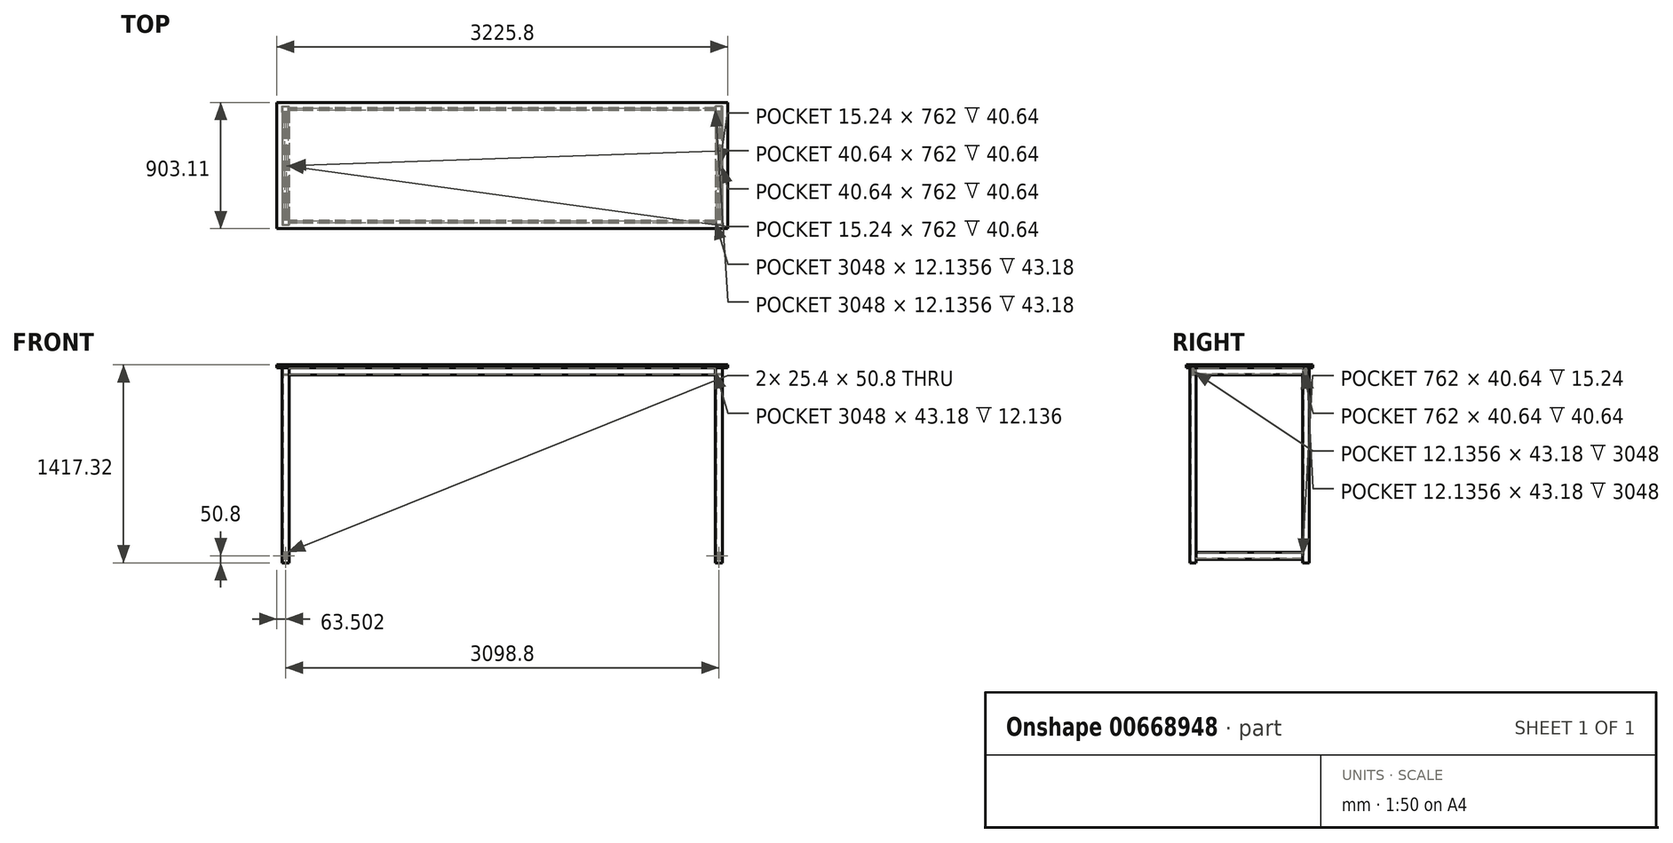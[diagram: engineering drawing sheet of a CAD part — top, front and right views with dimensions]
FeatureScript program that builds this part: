
annotation { "Feature Type Name" : "Feature", "Feature Type Description" : "" }
export const myFeature = defineFeature(function(context is Context, id is Id, definition is map)
    precondition{}
    {
        {
            var Q0;
            Q0=qCreatedBy(makeId("Top.planeOp"),FACE);
            var sketch = newSketch(context, id + "F0", { "sketchPlane" : qUnion([Q0])});
            skLineSegment(sketch, "E0.bottom", {"start": v(-52.67, 8.27) * mm, "end": v(-1.87, 8.27) * mm});
            skLineSegment(sketch, "E0.top", {"start": v(-52.67, -36.88) * mm, "end": v(-1.87, -36.88) * mm});
            skLineSegment(sketch, "E0.left", {"start": v(-52.67, 8.27) * mm, "end": v(-52.67, -36.88) * mm});
            skLineSegment(sketch, "E0.right", {"start": v(-1.87, 8.27) * mm, "end": v(-1.87, -36.88) * mm});
            skLineSegment(sketch, "E1.bottom", {"start": v(-47.59, 3.2) * mm, "end": v(-6.95, 3.2) * mm});
            skLineSegment(sketch, "E1.top", {"start": v(-47.59, -31.8) * mm, "end": v(-6.95, -31.8) * mm});
            skLineSegment(sketch, "E1.left", {"start": v(-47.59, 3.2) * mm, "end": v(-47.59, -31.8) * mm});
            skLineSegment(sketch, "E1.right", {"start": v(-6.95, 3.2) * mm, "end": v(-6.95, -31.8) * mm});
            skSolve(sketch);
        }
        {
            var Q0;
            Q0=makeQuery(id+"F0.imprint","IMPRINT",FACE,{"disambiguationData":[TD([[makeQuery(id+"F0.imprint","IMPRINT",EDGE,{"derivedFrom":sQuery(id+"F0.wireOp",EDGE,"E0.bottom")}),-1.0]])]});
            extrude(context, id + "F1", {"entities" : qUnion([Q0]), "depth" : 1397 * mm, "offsetDistance" : 25.4 * mm});
        }
        {
            var Q0;
            Q0=makeQuery(id+"F1.opExtrude","SWEPT_FACE",FACE,{"disambiguationData":[OSD([sQuery(id+"F0.wireOp",EDGE,"E0.bottom")])]});
            var sketch = newSketch(context, id + "F2", { "sketchPlane" : qUnion([Q0])});
            skLineSegment(sketch, "E2.bottom", {"start": v(14.57, 76.2) * mm, "end": v(39.97, 76.2) * mm});
            skLineSegment(sketch, "E2.top", {"start": v(14.57, 25.4) * mm, "end": v(39.97, 25.4) * mm});
            skLineSegment(sketch, "E2.left", {"start": v(14.57, 76.2) * mm, "end": v(14.57, 25.4) * mm});
            skLineSegment(sketch, "E2.right", {"start": v(39.97, 76.2) * mm, "end": v(39.97, 25.4) * mm});
            skLineSegment(sketch, "E3.bottom", {"start": v(19.65, 71.12) * mm, "end": v(34.89, 71.12) * mm});
            skLineSegment(sketch, "E3.top", {"start": v(19.65, 30.48) * mm, "end": v(34.89, 30.48) * mm});
            skLineSegment(sketch, "E3.left", {"start": v(19.65, 71.12) * mm, "end": v(19.65, 30.48) * mm});
            skLineSegment(sketch, "E3.right", {"start": v(34.89, 71.12) * mm, "end": v(34.89, 30.48) * mm});
            skLineSegment(sketch, "E4.bottom", {"start": v(52.67, 1397) * mm, "end": v(1.87, 1397) * mm});
            skLineSegment(sketch, "E4.top", {"start": v(52.67, 1346.2) * mm, "end": v(1.87, 1346.2) * mm});
            skLineSegment(sketch, "E4.left", {"start": v(52.67, 1397) * mm, "end": v(52.67, 1346.2) * mm});
            skLineSegment(sketch, "E4.right", {"start": v(1.87, 1397) * mm, "end": v(1.87, 1346.2) * mm});
            skLineSegment(sketch, "E5.bottom", {"start": v(47.59, 1391.92) * mm, "end": v(6.95, 1391.92) * mm});
            skLineSegment(sketch, "E5.top", {"start": v(47.59, 1351.28) * mm, "end": v(6.95, 1351.28) * mm});
            skLineSegment(sketch, "E5.left", {"start": v(47.59, 1391.92) * mm, "end": v(47.59, 1351.28) * mm});
            skLineSegment(sketch, "E5.right", {"start": v(6.95, 1391.92) * mm, "end": v(6.95, 1351.28) * mm});
            skSolve(sketch);
        }
        {
            var Q0;
            Q0=makeQuery(id+"F2.imprint","IMPRINT",FACE,{"disambiguationData":[TD([[makeQuery(id+"F2.imprint","IMPRINT",EDGE,{"derivedFrom":sQuery(id+"F2.wireOp",EDGE,"E2.bottom")}),-1.0]])]});
            var Q1;
            Q1=makeQuery(id+"F2.imprint","IMPRINT",FACE,{"disambiguationData":[TD([[makeQuery(id+"F2.imprint","IMPRINT",EDGE,{"derivedFrom":sQuery(id+"F2.wireOp",EDGE,"E4.bottom")}),1.0]])]});
            extrude(context, id + "F3", {"entities" : qUnion([Q0, Q1]), "operationType" : NewBodyOperationType.ADD, "depth" : 381 * mm, "offsetDistance" : 25.4 * mm});
        }
        {
            var Q0;
            Q0=makeQuery(id+"F3.boolean.opBoolean","MERGE",FACE,{"derivedFrom":[makeQuery(id+"F1.opExtrude","SWEPT_FACE",FACE,{"disambiguationData":[OSD([sQuery(id+"F0.wireOp",EDGE,"E0.right")])]}),makeQuery(id+"F3.opExtrude","SWEPT_FACE",FACE,{"disambiguationData":[OSD([sQuery(id+"F2.wireOp",EDGE,"E4.right")])]})]});
            var sketch = newSketch(context, id + "F4", { "sketchPlane" : qUnion([Q0])});
            skLineSegment(sketch, "E6.bottom", {"start": v(-24.18, 1397) * mm, "end": v(-4.43, 1397) * mm});
            skLineSegment(sketch, "E6.top", {"start": v(-24.18, 1346.2) * mm, "end": v(-4.43, 1346.2) * mm});
            skLineSegment(sketch, "E6.left", {"start": v(-24.18, 1397) * mm, "end": v(-24.18, 1346.2) * mm});
            skLineSegment(sketch, "E6.right", {"start": v(-4.43, 1397) * mm, "end": v(-4.43, 1346.2) * mm});
            skLineSegment(sketch, "E7.bottom", {"start": v(-20.37, 1393.2) * mm, "end": v(-8.24, 1393.2) * mm});
            skLineSegment(sketch, "E7.top", {"start": v(-20.37, 1350.01) * mm, "end": v(-8.24, 1350.01) * mm});
            skLineSegment(sketch, "E7.left", {"start": v(-20.37, 1393.2) * mm, "end": v(-20.37, 1350.01) * mm});
            skLineSegment(sketch, "E7.right", {"start": v(-8.24, 1393.2) * mm, "end": v(-8.24, 1350.01) * mm});
            skSolve(sketch);
        }
        {
            var Q0;
            Q0=makeQuery(id+"F4.imprint","IMPRINT",FACE,{"disambiguationData":[TD([[makeQuery(id+"F4.imprint","IMPRINT",EDGE,{"derivedFrom":sQuery(id+"F4.wireOp",EDGE,"E6.bottom")}),1.0]])]});
            extrude(context, id + "F5", {"entities" : qUnion([Q0]), "operationType" : NewBodyOperationType.ADD, "depth" : 1524 * mm, "offsetDistance" : 25.4 * mm});
        }
        {
            var Q0;
            Q0=makeQuery(id+"F1.opExtrude","SWEPT_BODY",BODY,{"disambiguationData":[OSD([sQuery(id+"F0.wireOp",EDGE,"E0.bottom"),sQuery(id+"F0.wireOp",EDGE,"E0.top"),sQuery(id+"F0.wireOp",EDGE,"E0.left"),sQuery(id+"F0.wireOp",EDGE,"E0.right"),sQuery(id+"F0.wireOp",EDGE,"E1.bottom"),sQuery(id+"F0.wireOp",EDGE,"E1.top"),sQuery(id+"F0.wireOp",EDGE,"E1.left"),sQuery(id+"F0.wireOp",EDGE,"E1.right")])]});
            var Q1;
            Q1=makeQuery(id+"F5.opExtrude","CAP_FACE",FACE,{"disambiguationData":[OSD([sQuery(id+"F4.wireOp",EDGE,"E6.bottom"),sQuery(id+"F4.wireOp",EDGE,"E6.top"),sQuery(id+"F4.wireOp",EDGE,"E6.left"),sQuery(id+"F4.wireOp",EDGE,"E6.right"),sQuery(id+"F4.wireOp",EDGE,"E7.bottom"),sQuery(id+"F4.wireOp",EDGE,"E7.top"),sQuery(id+"F4.wireOp",EDGE,"E7.left"),sQuery(id+"F4.wireOp",EDGE,"E7.right")])],"isStart":false});
            mirror(context, id + "F6", {"operationType" : NewBodyOperationType.ADD, "entities" : qUnion([Q0]), "mirrorPlane" : qUnion([Q1])});
        }
        {
            var Q0;
            Q0=makeQuery(id+"F1.opExtrude","SWEPT_BODY",BODY,{"disambiguationData":[OSD([sQuery(id+"F0.wireOp",EDGE,"E0.bottom"),sQuery(id+"F0.wireOp",EDGE,"E0.top"),sQuery(id+"F0.wireOp",EDGE,"E0.left"),sQuery(id+"F0.wireOp",EDGE,"E0.right"),sQuery(id+"F0.wireOp",EDGE,"E1.bottom"),sQuery(id+"F0.wireOp",EDGE,"E1.top"),sQuery(id+"F0.wireOp",EDGE,"E1.left"),sQuery(id+"F0.wireOp",EDGE,"E1.right")])]});
            var Q1;
            Q1=makeQuery(id+"F3.opExtrude","CAP_FACE",FACE,{"disambiguationData":[OSD([sQuery(id+"F2.wireOp",EDGE,"E4.bottom"),sQuery(id+"F2.wireOp",EDGE,"E4.top"),sQuery(id+"F2.wireOp",EDGE,"E4.left"),sQuery(id+"F2.wireOp",EDGE,"E4.right"),sQuery(id+"F2.wireOp",EDGE,"E5.bottom"),sQuery(id+"F2.wireOp",EDGE,"E5.top"),sQuery(id+"F2.wireOp",EDGE,"E5.left"),sQuery(id+"F2.wireOp",EDGE,"E5.right")])],"isStart":false});
            mirror(context, id + "F7", {"operationType" : NewBodyOperationType.ADD, "entities" : qUnion([Q0]), "mirrorPlane" : qUnion([Q1])});
        }
        {
            var Q0;
            {var subQ0=makeQuery(id+"F5.boolean.opBoolean","MERGE",FACE,{"derivedFrom":[makeQuery(id+"F3.boolean.opBoolean","MERGE",FACE,{"derivedFrom":[makeQuery(id+"F1.opExtrude","CAP_FACE",FACE,{"disambiguationData":[OSD([sQuery(id+"F0.wireOp",EDGE,"E0.bottom"),sQuery(id+"F0.wireOp",EDGE,"E0.top"),sQuery(id+"F0.wireOp",EDGE,"E0.left"),sQuery(id+"F0.wireOp",EDGE,"E0.right"),sQuery(id+"F0.wireOp",EDGE,"E1.bottom"),sQuery(id+"F0.wireOp",EDGE,"E1.top"),sQuery(id+"F0.wireOp",EDGE,"E1.left"),sQuery(id+"F0.wireOp",EDGE,"E1.right")])],"isStart":false}),makeQuery(id+"F3.opExtrude","SWEPT_FACE",FACE,{"disambiguationData":[OSD([sQuery(id+"F2.wireOp",EDGE,"E4.bottom")])]})]}),makeQuery(id+"F5.opExtrude","SWEPT_FACE",FACE,{"disambiguationData":[OSD([sQuery(id+"F4.wireOp",EDGE,"E6.bottom")])]})]});var subQ1=makeQuery(id+"F6.boolean.opBoolean","MERGE",FACE,{"derivedFrom":[subQ0,makeQuery(id+"F6.opPattern","COPY",FACE,{"derivedFrom":subQ0,"instanceName":"1"})]});Q0=makeQuery(id+"F7.boolean.opBoolean","MERGE",FACE,{"derivedFrom":[subQ1,makeQuery(id+"F7.opPattern","COPY",FACE,{"derivedFrom":subQ1,"instanceName":"1"})]});}
            var sketch = newSketch(context, id + "F8", { "sketchPlane" : qUnion([Q0])});
            skLineSegment(sketch, "E8.bottom", {"start": v(3135.03, -62.28) * mm, "end": v(-90.77, -62.28) * mm});
            skLineSegment(sketch, "E8.top", {"start": v(3135.03, 840.83) * mm, "end": v(-90.77, 840.83) * mm});
            skLineSegment(sketch, "E8.left", {"start": v(3135.03, -62.28) * mm, "end": v(3135.03, 840.83) * mm});
            skLineSegment(sketch, "E8.right", {"start": v(-90.77, -62.28) * mm, "end": v(-90.77, 840.83) * mm});
            skSolve(sketch);
        }
        {
            var Q0;
            Q0=makeQuery(id+"F8.imprint","IMPRINT",FACE,{"disambiguationData":[TD([[makeQuery(id+"F8.imprint","IMPRINT",EDGE,{"derivedFrom":sQuery(id+"F8.wireOp",EDGE,"E8.bottom")}),-1.0]])]});
            var Q1;
            {var subQ3=sQuery(id+"F0.wireOp",EDGE,"E0.top");var subQ4=makeQuery(id+"F1.opExtrude","CAP_EDGE",EDGE,{"disambiguationData":[OSD([subQ3])],"isStart":false});Q1=makeQuery(id+"F8.imprint","IMPRINT",FACE,{"disambiguationData":[TD([[makeQuery(id+"F8.imprint","IMPRINT",EDGE,{"derivedFrom":subQ4}),1.0]])]});}
            var Q2;
            {var subQ0=sQuery(id+"F4.wireOp",EDGE,"E6.right");var subQ1=sQuery(id+"F4.wireOp",EDGE,"E6.bottom");var subQ2=sQuery(id+"F2.wireOp",EDGE,"E4.right");var subQ3=sQuery(id+"F2.wireOp",EDGE,"E4.bottom");var subQ4=sQuery(id+"F0.wireOp",EDGE,"E0.right");var subQ5=makeQuery(id+"F5.opExtrude","SWEPT_EDGE",EDGE,{"disambiguationData":[OSD([subQ4,subQ3,subQ2,subQ1,subQ0])]});var subQ6=makeQuery(id+"F6.boolean.opBoolean","MERGE",EDGE,{"derivedFrom":[subQ5,makeQuery(id+"F6.opPattern","COPY",EDGE,{"derivedFrom":subQ5,"instanceName":"1"})]});Q2=makeQuery(id+"F8.imprint","IMPRINT",FACE,{"disambiguationData":[TD([[makeQuery(id+"F8.imprint","IMPRINT",EDGE,{"derivedFrom":subQ6}),-1.0]])]});}
            var Q3;
            Q3=makeQuery(id+"F8.imprint","IMPRINT",FACE,{"disambiguationData":[TD([[makeQuery(id+"F8.imprint","IMPRINT",EDGE,{"derivedFrom":makeQuery(id+"F1.opExtrude","CAP_EDGE",EDGE,{"disambiguationData":[OSD([sQuery(id+"F0.wireOp",EDGE,"E1.bottom")])],"isStart":false})}),-1.0]])]});
            var Q4;
            Q4=makeQuery(id+"F8.imprint","IMPRINT",FACE,{"disambiguationData":[TD([[makeQuery(id+"F8.imprint","IMPRINT",EDGE,{"derivedFrom":makeQuery(id+"F7.opPattern","COPY",EDGE,{"derivedFrom":makeQuery(id+"F1.opExtrude","CAP_EDGE",EDGE,{"disambiguationData":[OSD([sQuery(id+"F0.wireOp",EDGE,"E1.bottom")])],"isStart":false}),"instanceName":"1"})}),1.0]])]});
            var Q5;
            Q5=makeQuery(id+"F8.imprint","IMPRINT",FACE,{"disambiguationData":[TD([[makeQuery(id+"F8.imprint","IMPRINT",EDGE,{"derivedFrom":makeQuery(id+"F6.opPattern","COPY",EDGE,{"derivedFrom":makeQuery(id+"F1.opExtrude","CAP_EDGE",EDGE,{"disambiguationData":[OSD([sQuery(id+"F0.wireOp",EDGE,"E1.bottom")])],"isStart":false}),"instanceName":"1"})}),1.0]])]});
            var Q6;
            Q6=makeQuery(id+"F8.imprint","IMPRINT",FACE,{"disambiguationData":[TD([[makeQuery(id+"F8.imprint","IMPRINT",EDGE,{"derivedFrom":makeQuery(id+"F7.opPattern","COPY",EDGE,{"derivedFrom":makeQuery(id+"F6.opPattern","COPY",EDGE,{"derivedFrom":makeQuery(id+"F1.opExtrude","CAP_EDGE",EDGE,{"disambiguationData":[OSD([sQuery(id+"F0.wireOp",EDGE,"E1.bottom")])],"isStart":false}),"instanceName":"1"}),"instanceName":"1"})}),-1.0]])]});
            extrude(context, id + "F9", {"entities" : qUnion([Q0, Q1, Q2, Q3, Q4, Q5, Q6]), "operationType" : NewBodyOperationType.ADD, "depth" : 20.32 * mm, "offsetDistance" : 25.4 * mm});
        }
    });
